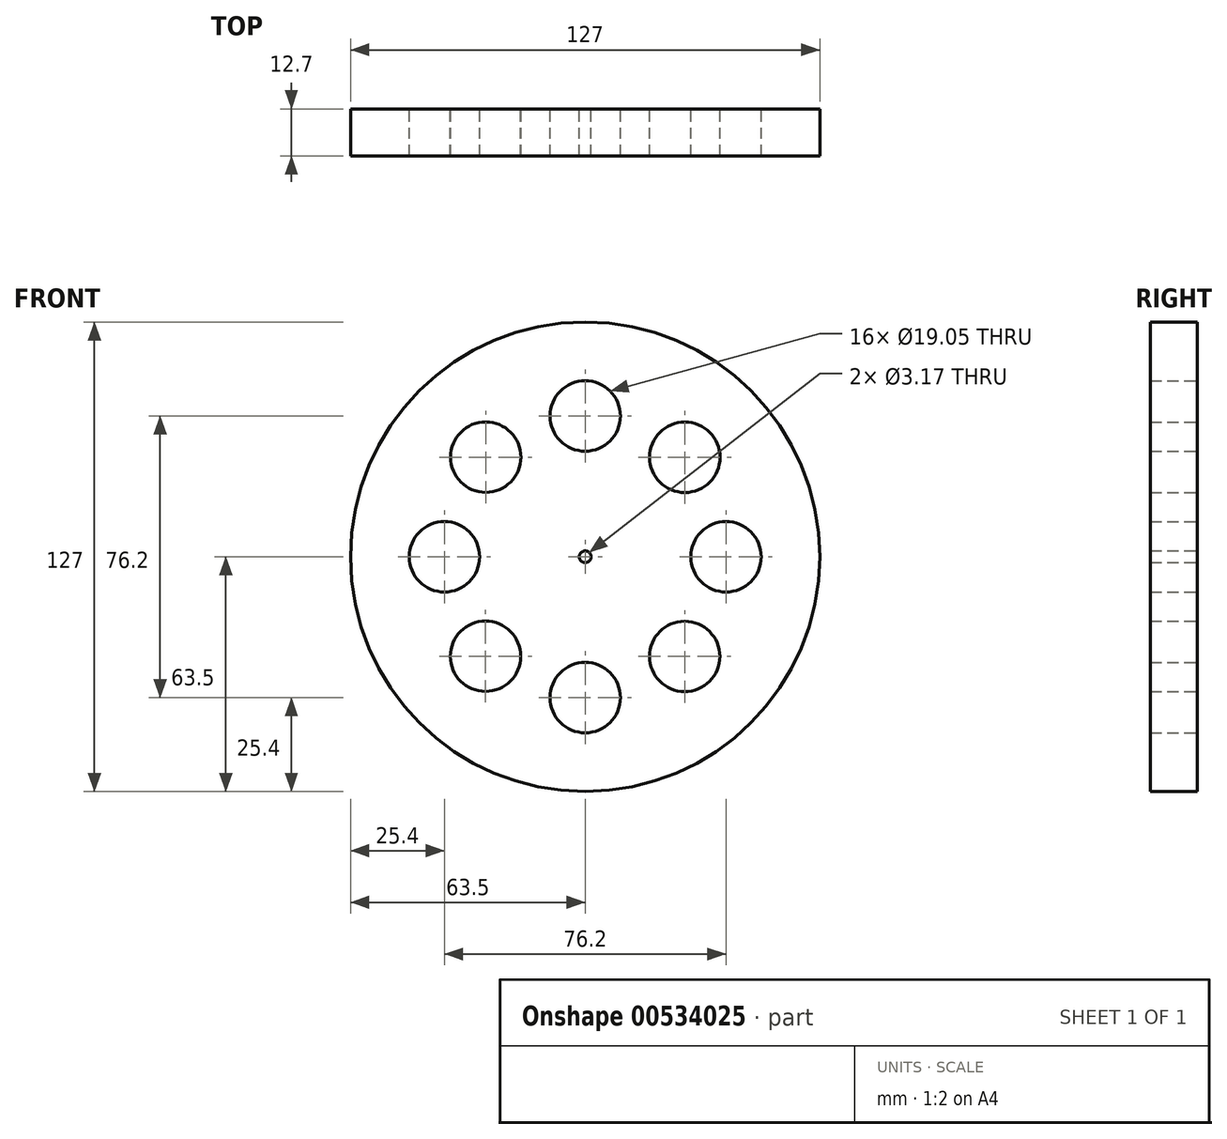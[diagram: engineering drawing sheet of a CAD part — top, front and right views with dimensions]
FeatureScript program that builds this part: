
annotation { "Feature Type Name" : "Feature", "Feature Type Description" : "" }
export const myFeature = defineFeature(function(context is Context, id is Id, definition is map)
    precondition{}
    {
        {
            var Q0;
            Q0=qCreatedBy(makeId("Front.planeOp"),FACE);
            var sketch = newSketch(context, id + "F0", { "sketchPlane" : qUnion([Q0])});
            skCircle(sketch, "E0", {"center": v(0, 0) * mm, "radius": 63.5 * mm});
            skCircle(sketch, "E1", {"center": v(-26.92, 26.96) * mm, "radius": 9.53 * mm});
            skCircle(sketch, "E2", {"center": v(0, 38.1) * mm, "radius": 9.53 * mm});
            skCircle(sketch, "E3", {"center": v(26.96, 26.92) * mm, "radius": 9.53 * mm});
            skCircle(sketch, "E4", {"center": v(38.1, 0) * mm, "radius": 9.53 * mm});
            skCircle(sketch, "E5", {"center": v(26.92, -26.96) * mm, "radius": 9.53 * mm});
            skCircle(sketch, "E6", {"center": v(0, -38.1) * mm, "radius": 9.53 * mm});
            skCircle(sketch, "E7", {"center": v(-26.96, -26.92) * mm, "radius": 9.53 * mm});
            skCircle(sketch, "E8", {"center": v(-38.1, 0) * mm, "radius": 9.53 * mm});
            skCircle(sketch, "E9", {"center": v(0, 0) * mm, "radius": 1.59 * mm});
            skSolve(sketch);
        }
        {
            var Q0;
            Q0=makeQuery(id+"F0.imprint","IMPRINT",FACE,{"disambiguationData":[TD([[makeQuery(id+"F0.imprint","IMPRINT",EDGE,{"derivedFrom":sQuery(id+"F0.wireOp",EDGE,"E0")}),1.0]])]});
            extrude(context, id + "F1", {"entities" : qUnion([Q0]), "depth" : 12.7 * mm, "offsetDistance" : 25.4 * mm});
        }
    });
